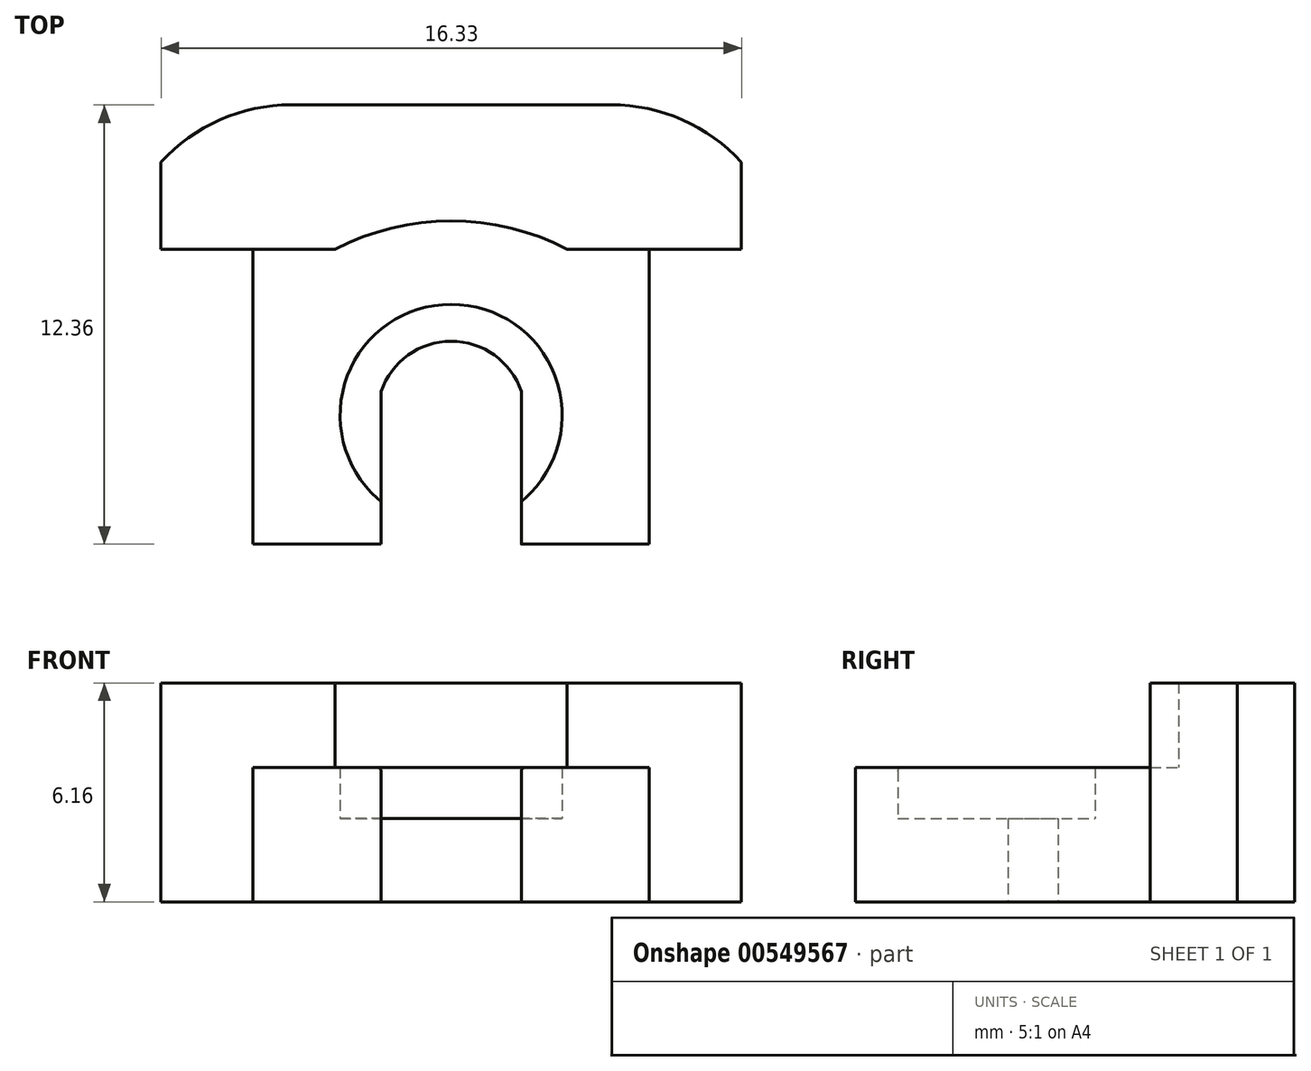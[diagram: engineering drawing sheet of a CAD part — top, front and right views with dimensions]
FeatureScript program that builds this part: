
annotation { "Feature Type Name" : "Feature", "Feature Type Description" : "" }
export const myFeature = defineFeature(function(context is Context, id is Id, definition is map)
    precondition{}
    {
        {
            var Q0;
            Q0=qCreatedBy(makeId("Top.planeOp"),FACE);
            var sketch = newSketch(context, id + "F0", { "sketchPlane" : qUnion([Q0])});
            skLineSegment(sketch, "E0", {"start": v(4.28, 2.34) * mm, "end": v(4.28, -5.96) * mm});
            skLineSegment(sketch, "E1", {"start": v(4.28, -5.96) * mm, "end": v(0.68, -5.96) * mm});
            skLineSegment(sketch, "E2", {"start": v(0.68, -5.96) * mm, "end": v(0.68, -1.67) * mm});
            skArc(sketch, "E3", {"start": v(0.68, -1.67) * mm, "mid": v(-1.3, -0.25) * mm, "end": v(-3.27, -1.67) * mm});
            skLineSegment(sketch, "E4", {"start": v(-6.87, -5.96) * mm, "end": v(-6.87, 2.34) * mm});
            skLineSegment(sketch, "E5", {"start": v(-3.27, -1.67) * mm, "end": v(-3.27, -5.96) * mm});
            skLineSegment(sketch, "E6", {"start": v(-3.27, -5.96) * mm, "end": v(-6.87, -5.96) * mm});
            skLineSegment(sketch, "E7", {"start": v(4.28, 2.34) * mm, "end": v(6.87, 2.34) * mm});
            skLineSegment(sketch, "E8", {"start": v(6.87, 2.34) * mm, "end": v(6.87, 4.8) * mm});
            skLineSegment(sketch, "E9", {"start": v(3.2, 6.4) * mm, "end": v(-5.8, 6.4) * mm});
            skLineSegment(sketch, "E10", {"start": v(-9.46, 4.8) * mm, "end": v(-9.46, 2.34) * mm});
            skLineSegment(sketch, "E11", {"start": v(-9.46, 2.34) * mm, "end": v(-6.87, 2.34) * mm});
            skLineSegment(sketch, "E12", {"start": v(-1.3, 3.13) * mm, "end": v(-1.3, 6.4) * mm});
            skCircle(sketch, "E13", {"center": v(-1.3, -2.33) * mm, "radius": 3.12 * mm});
            skLineSegment(sketch, "E14", {"start": v(-9.46, 4.8) * mm, "end": v(6.87, 4.8) * mm});
            skLineSegment(sketch, "E15", {"start": v(-6.87, 2.34) * mm, "end": v(-4.56, 2.34) * mm});
            skLineSegment(sketch, "E16", {"start": v(4.28, 2.34) * mm, "end": v(1.97, 2.34) * mm});
            skArc(sketch, "E17", {"start": v(1.97, 2.34) * mm, "mid": v(-1.3, 3.13) * mm, "end": v(-4.56, 2.34) * mm});
            skArc(sketch, "E18", {"start": v(-5.8, 6.4) * mm, "mid": v(-7.8, 5.98) * mm, "end": v(-9.46, 4.8) * mm});
            skArc(sketch, "E19", {"start": v(6.87, 4.8) * mm, "mid": v(5.2, 5.98) * mm, "end": v(3.2, 6.4) * mm});
            skSolve(sketch);
        }
        {
            var Q0;
            {var subQ0=sQuery(id+"F0.wireOp",EDGE,"E3");Q0=makeQuery(id+"F0.imprint","IMPRINT",FACE,{"disambiguationData":[TD([[makeQuery(id+"F0.imprint","IMPRINT",EDGE,{"derivedFrom":subQ0}),-1.0]])]});}
            extrude(context, id + "F1", {"entities" : qUnion([Q0]), "depth" : 2.35 * mm, "offsetDistance" : 25 * mm});
        }
        {
            var Q0;
            Q0=makeQuery(id+"F0.imprint","IMPRINT",FACE,{"disambiguationData":[TD([[makeQuery(id+"F0.imprint","IMPRINT",EDGE,{"derivedFrom":sQuery(id+"F0.wireOp",EDGE,"E0")}),-1.0]])]});
            extrude(context, id + "F2", {"entities" : qUnion([Q0]), "operationType" : NewBodyOperationType.ADD, "depth" : 3.78 * mm, "offsetDistance" : 25 * mm});
        }
        {
            var Q0;
            {var subQ5=sQuery(id+"F0.wireOp",EDGE,"E10");Q0=makeQuery(id+"F0.imprint","IMPRINT",FACE,{"disambiguationData":[TD([[makeQuery(id+"F0.imprint","IMPRINT",EDGE,{"derivedFrom":subQ5}),1.0]])]});}
            var Q1;
            {var subQ0=sQuery(id+"F0.wireOp",EDGE,"24D2AZMy-OHpb-HDOf-qSfj-c9wEJu6qhqcY");Q1=makeQuery(id+"F0.imprint","IMPRINT",FACE,{"disambiguationData":[TD([[makeQuery(id+"F0.imprint","IMPRINT",EDGE,{"derivedFrom":subQ0}),1.0]])]});}
            var Q2;
            {var subQ0=sQuery(id+"F0.wireOp",EDGE,"ZlUy6x42-7Bzy-wT53-GEc0-OXN14umSX8JD");Q2=makeQuery(id+"F0.imprint","IMPRINT",FACE,{"disambiguationData":[TD([[makeQuery(id+"F0.imprint","IMPRINT",EDGE,{"derivedFrom":subQ0}),1.0]])]});}
            var Q3;
            Q3=makeQuery(id+"F0.imprint","IMPRINT",FACE,{"disambiguationData":[TD([[makeQuery(id+"F0.imprint","IMPRINT",EDGE,{"derivedFrom":sQuery(id+"F0.wireOp",EDGE,"E7")}),1.0]])]});
            var Q4;
            {var subQ1=sQuery(id+"F0.wireOp",EDGE,"E9");var subQ3=sQuery(id+"F0.wireOp",EDGE,"E12");var subQ4=makeQuery(id+"F0.imprint","INTERSECT",VERTEX,{"derivedFrom":[subQ1,subQ3]});Q4=makeQuery(id+"F0.imprint","IMPRINT",FACE,{"disambiguationData":[TD([[makeQuery(id+"F0.imprint","IMPRINT",EDGE,{"disambiguationData":[TD([[subQ4,1.0]])],"derivedFrom":subQ3}),-1.0]])]});}
            var Q5;
            {var subQ3=sQuery(id+"F0.wireOp",EDGE,"E16");Q5=makeQuery(id+"F0.imprint","IMPRINT",FACE,{"disambiguationData":[TD([[makeQuery(id+"F0.imprint","IMPRINT",EDGE,{"derivedFrom":subQ3}),-1.0]])]});}
            var Q6;
            {var subQ1=sQuery(id+"F0.wireOp",EDGE,"E9");var subQ3=sQuery(id+"F0.wireOp",EDGE,"E12");var subQ4=makeQuery(id+"F0.imprint","INTERSECT",VERTEX,{"derivedFrom":[subQ1,subQ3]});Q6=makeQuery(id+"F0.imprint","IMPRINT",FACE,{"disambiguationData":[TD([[makeQuery(id+"F0.imprint","IMPRINT",EDGE,{"disambiguationData":[TD([[subQ4,1.0]])],"derivedFrom":subQ3}),1.0]])]});}
            var Q7;
            {var subQ3=sQuery(id+"F0.wireOp",EDGE,"E15");Q7=makeQuery(id+"F0.imprint","IMPRINT",FACE,{"disambiguationData":[TD([[makeQuery(id+"F0.imprint","IMPRINT",EDGE,{"derivedFrom":subQ3}),1.0]])]});}
            var Q8;
            {var subQ0=sQuery(id+"F0.wireOp",EDGE,"pA4BLqO5-sNxH-NCEw-M5rz-PjrjKgtW8z8i");Q8=makeQuery(id+"F0.imprint","IMPRINT",FACE,{"disambiguationData":[TD([[makeQuery(id+"F0.imprint","IMPRINT",EDGE,{"derivedFrom":subQ0}),-1.0]])]});}
            var Q9;
            {var subQ0=sQuery(id+"F0.wireOp",EDGE,"e8zGusvV-8x8e-N4gG-y2Yn-J32Cbc1Bfkjy");Q9=makeQuery(id+"F0.imprint","IMPRINT",FACE,{"disambiguationData":[TD([[makeQuery(id+"F0.imprint","IMPRINT",EDGE,{"derivedFrom":subQ0}),-1.0]])]});}
            extrude(context, id + "F3", {"entities" : qUnion([Q0, Q1, Q2, Q3, Q4, Q5, Q6, Q7, Q8, Q9]), "operationType" : NewBodyOperationType.ADD, "depth" : 6.16 * mm, "offsetDistance" : 25 * mm});
        }
        {
            var Q0;
            Q0=makeQuery(id+"F2.opExtrude","CAP_EDGE",EDGE,{"disambiguationData":[OSD([sQuery(id+"F0.wireOp",EDGE,"E2")])],"isStart":false});
            fillet(context, id + "F4", {"entities" : qUnion([Q0]), "radius" : 0.1 * mm, "allowEdgeOverflow" : false});
        }
        {
            var Q0;
            Q0=makeQuery(id+"F2.opExtrude","CAP_EDGE",EDGE,{"disambiguationData":[OSD([sQuery(id+"F0.wireOp",EDGE,"E5")])],"isStart":false});
            fillet(context, id + "F5", {"entities" : qUnion([Q0]), "radius" : .1 * mm, "tangentPropagation" : true, "allowEdgeOverflow" : false});
        }
    });
